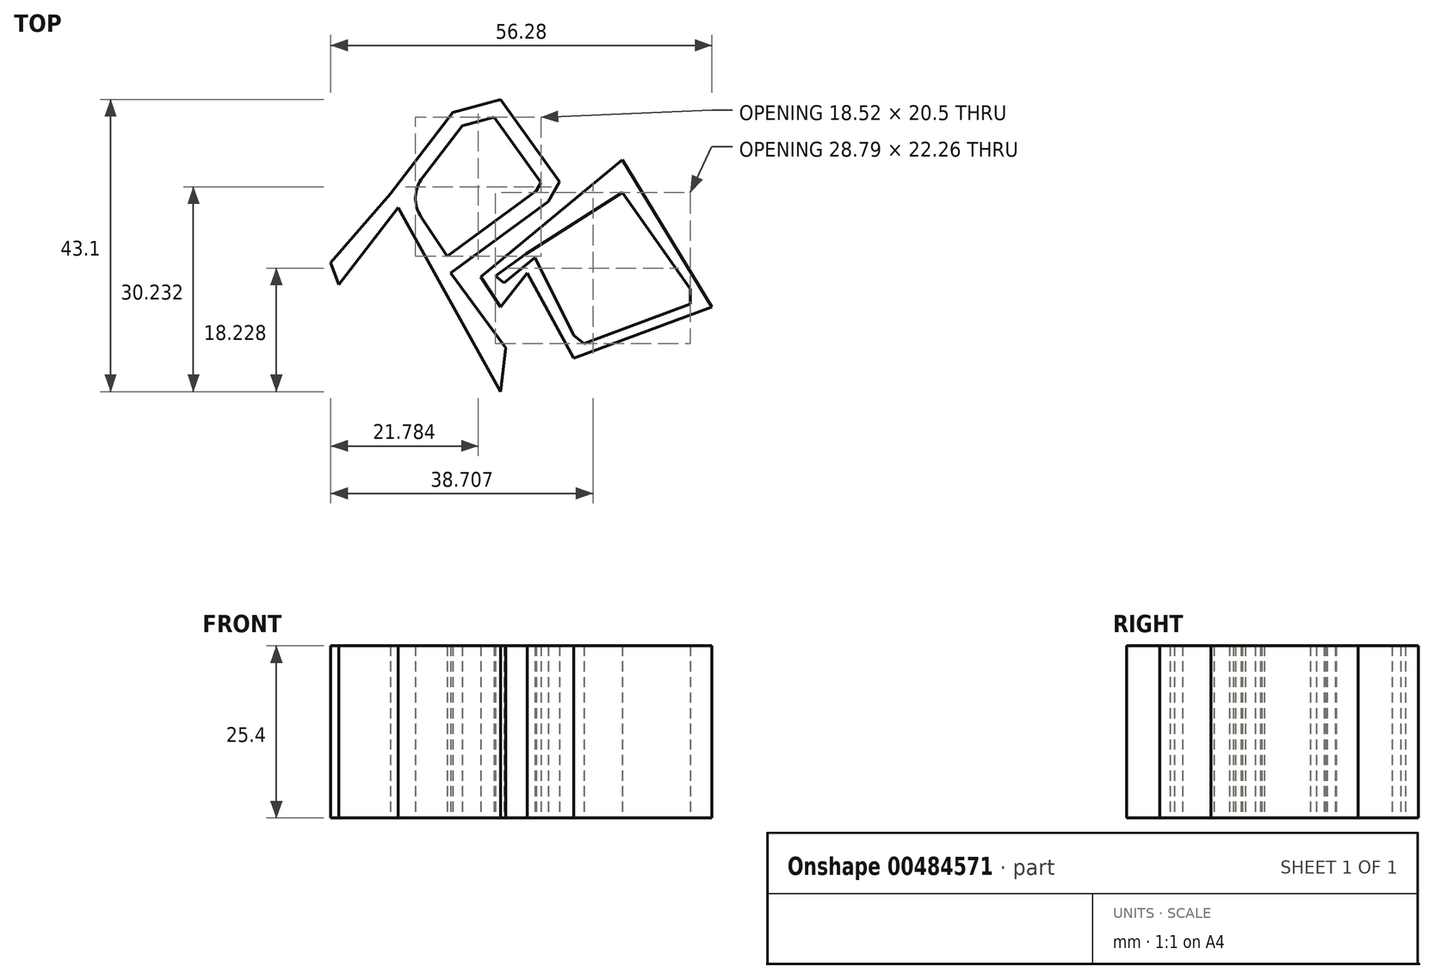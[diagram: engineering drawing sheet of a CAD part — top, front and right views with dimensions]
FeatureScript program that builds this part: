
annotation { "Feature Type Name" : "Feature", "Feature Type Description" : "" }
export const myFeature = defineFeature(function(context is Context, id is Id, definition is map)
    precondition{}
    {
        {
            var Q0;
            Q0=qCreatedBy(makeId("Top.planeOp"),FACE);
            var sketch = newSketch(context, id + "F0", { "sketchPlane" : qUnion([Q0])});
            skLineSegment(sketch, "E0", {"start": v(-7.9, -8.74) * mm, "end": v(-16.01, 2.35) * mm});
            skLineSegment(sketch, "E1", {"start": v(-16.01, 2.35) * mm, "end": v(-1.64, 12.87) * mm});
            skLineSegment(sketch, "E2", {"start": v(-1.64, 12.87) * mm, "end": v(0, 15.8) * mm});
            skLineSegment(sketch, "E3", {"start": v(0, 15.8) * mm, "end": v(-8.69, 27.92) * mm});
            skLineSegment(sketch, "E4", {"start": v(-8.69, 27.92) * mm, "end": v(-15.7, 26.02) * mm});
            skLineSegment(sketch, "E5", {"start": v(-15.7, 26.02) * mm, "end": v(-24.95, 13.99) * mm});
            skLineSegment(sketch, "E6", {"start": v(-23.82, 11.95) * mm, "end": v(-8.69, -15.18) * mm});
            skLineSegment(sketch, "E7", {"start": v(-8.69, -15.18) * mm, "end": v(-7.9, -8.74) * mm});
            skLineSegment(sketch, "E8", {"start": v(-11.57, 1.75) * mm, "end": v(9.32, 19.04) * mm});
            skLineSegment(sketch, "E9", {"start": v(9.32, 19.04) * mm, "end": v(22.53, -2.7) * mm});
            skLineSegment(sketch, "E10", {"start": v(22.53, -2.7) * mm, "end": v(2.12, -10.26) * mm});
            skLineSegment(sketch, "E11", {"start": v(2.12, -10.26) * mm, "end": v(-4.72, 2.35) * mm});
            skLineSegment(sketch, "E12", {"start": v(-4.72, 2.35) * mm, "end": v(-8.69, -2.7) * mm});
            skLineSegment(sketch, "E13", {"start": v(-8.69, -2.7) * mm, "end": v(-11.57, 1.75) * mm});
            skLineSegment(sketch, "E14", {"start": v(-24.95, 13.99) * mm, "end": v(-33.75, 3.86) * mm});
            skLineSegment(sketch, "E15", {"start": v(-33.75, 3.86) * mm, "end": v(-32.54, 0.6) * mm});
            skLineSegment(sketch, "E16", {"start": v(-32.54, 0.6) * mm, "end": v(-23.82, 11.95) * mm});
            skLineSegment(sketch, "E17.0", {"start": v(-14.36, 24.02) * mm, "end": v(-22.4, 13.55) * mm});
            skLineSegment(sketch, "E17.1", {"start": v(-16.53, 4.8) * mm, "end": v(-3.4, 14.42) * mm});
            skLineSegment(sketch, "E17.2", {"start": v(-3.4, 14.42) * mm, "end": v(-2.7, 15.65) * mm});
            skLineSegment(sketch, "E17.3", {"start": v(-2.7, 15.65) * mm, "end": v(-9.62, 25.3) * mm});
            skLineSegment(sketch, "E17.4", {"start": v(-9.62, 25.3) * mm, "end": v(-14.36, 24.02) * mm});
            skLineSegment(sketch, "E18", {"start": v(-16.53, 4.8) * mm, "end": v(-22.4, 13.55) * mm});
            skLineSegment(sketch, "E19", {"start": v(2.13, -6.88) * mm, "end": v(3.66, -8.08) * mm});
            skLineSegment(sketch, "E20", {"start": v(3.66, -8.08) * mm, "end": v(19.35, -2.27) * mm});
            skLineSegment(sketch, "E21", {"start": v(19.35, -2.27) * mm, "end": v(19.35, 0) * mm});
            skLineSegment(sketch, "E22", {"start": v(19.35, 0) * mm, "end": v(9.27, 14.18) * mm});
            skLineSegment(sketch, "E23", {"start": v(9.27, 14.18) * mm, "end": v(-4.87, 5.18) * mm});
            skLineSegment(sketch, "E24", {"start": v(-4.87, 5.18) * mm, "end": v(-9.44, 1.9) * mm});
            skLineSegment(sketch, "E25", {"start": v(-9.44, 1.9) * mm, "end": v(-8.15, 0.89) * mm});
            skLineSegment(sketch, "E26", {"start": v(-8.15, 0.89) * mm, "end": v(-3.58, 4.61) * mm});
            skLineSegment(sketch, "E27", {"start": v(-3.58, 4.61) * mm, "end": v(2.13, -6.88) * mm});
            skLineSegment(sketch, "E28", {"start": v(-41.15, -4.64) * mm, "end": v(29.13, -28.62) * mm});
            skLineSegment(sketch, "E29.MirrorCS", {"start": v(-22.92, -42.8) * mm, "end": v(-23.12, -44.2) * mm});
            skLineSegment(sketch, "E30.MirrorCS", {"start": v(-20.05, -29.2) * mm, "end": v(-18.41, -29.19) * mm});
            skLineSegment(sketch, "E31.MirrorCS", {"start": v(-5.53, -29.32) * mm, "end": v(-3.58, -29.3) * mm});
            skLineSegment(sketch, "E32.MirrorCS", {"start": v(-12.33, -21.72) * mm, "end": v(-25.53, -25.54) * mm});
            skLineSegment(sketch, "E33.MirrorCS", {"start": v(-25.53, -25.54) * mm, "end": v(-20.58, -42.65) * mm});
            skLineSegment(sketch, "E34.MirrorCS", {"start": v(-21.08, -45.97) * mm, "end": v(-35.36, -50.26) * mm});
            skLineSegment(sketch, "E35.MirrorCS", {"start": v(-27.44, -27.16) * mm, "end": v(-37.43, -30.5) * mm});
            skLineSegment(sketch, "E36.MirrorCS", {"start": v(-37.58, -28.37) * mm, "end": v(-9.02, -16.14) * mm});
            skLineSegment(sketch, "E37.MirrorCS", {"start": v(-9.02, -16.14) * mm, "end": v(-12.33, -21.72) * mm});
            skLineSegment(sketch, "E38.MirrorCS", {"start": v(-3.47, -26.64) * mm, "end": v(-16.6, -32.44) * mm});
            skLineSegment(sketch, "E39.MirrorCS", {"start": v(-17.08, -34.93) * mm, "end": v(-5.53, -29.32) * mm});
            skLineSegment(sketch, "E40.MirrorCS", {"start": v(-37.54, -14.05) * mm, "end": v(-37.58, -28.37) * mm});
            skLineSegment(sketch, "E41.MirrorCS", {"start": v(-18.44, -34.6) * mm, "end": v(-20.05, -29.2) * mm});
            skLineSegment(sketch, "E42.MirrorCS", {"start": v(-3.58, -29.3) * mm, "end": v(5.28, -43.5) * mm});
            skLineSegment(sketch, "E43.MirrorCS", {"start": v(-37.46, -43.7) * mm, "end": v(-37.43, -30.5) * mm});
            skLineSegment(sketch, "E44.MirrorCS", {"start": v(-16.65, -26.02) * mm, "end": v(-21.64, -27.78) * mm});
            skLineSegment(sketch, "E45.MirrorCS", {"start": v(5.28, -43.5) * mm, "end": v(3.9, -45.3) * mm});
            skLineSegment(sketch, "E46.MirrorCS", {"start": v(-40.49, -15.89) * mm, "end": v(-37.54, -14.05) * mm});
            skLineSegment(sketch, "E47.MirrorCS", {"start": v(-27.44, -27.16) * mm, "end": v(-22.92, -42.8) * mm});
            skLineSegment(sketch, "E48.MirrorCS", {"start": v(-20.58, -42.65) * mm, "end": v(-21.08, -45.97) * mm});
            skLineSegment(sketch, "E49.MirrorCS", {"start": v(-39.71, -29.29) * mm, "end": v(-40.49, -15.89) * mm});
            skLineSegment(sketch, "E50.MirrorCS", {"start": v(3.9, -45.3) * mm, "end": v(-12.75, -50.35) * mm});
            skLineSegment(sketch, "E51.MirrorCS", {"start": v(-35.36, -50.26) * mm, "end": v(-39.75, -44.47) * mm});
            skLineSegment(sketch, "E52.MirrorCS", {"start": v(-39.75, -44.47) * mm, "end": v(-39.71, -29.29) * mm});
            skLineSegment(sketch, "E53.MirrorCS", {"start": v(-21.64, -27.78) * mm, "end": v(-15.68, -54.23) * mm});
            skLineSegment(sketch, "E54.MirrorCS", {"start": v(-15.68, -54.23) * mm, "end": v(8.06, -45.1) * mm});
            skLineSegment(sketch, "E55.MirrorCS", {"start": v(8.06, -45.1) * mm, "end": v(-3.47, -26.64) * mm});
            skLineSegment(sketch, "E56.MirrorCS", {"start": v(-12.75, -50.35) * mm, "end": v(-18.44, -34.6) * mm});
            skLineSegment(sketch, "E57.MirrorCS", {"start": v(-16.6, -32.44) * mm, "end": v(-16.65, -26.02) * mm});
            skLineSegment(sketch, "E58.MirrorCS", {"start": v(-23.12, -44.2) * mm, "end": v(-34.5, -47.6) * mm});
            skLineSegment(sketch, "E59.MirrorCS", {"start": v(-34.5, -47.6) * mm, "end": v(-37.46, -43.7) * mm});
            skLineSegment(sketch, "E60.MirrorCS", {"start": v(-18.41, -29.19) * mm, "end": v(-17.08, -34.93) * mm});
            skSolve(sketch);
        }
        {
            var Q0;
            Q0=makeQuery(id+"F0.imprint","IMPRINT",FACE,{"disambiguationData":[TD([[makeQuery(id+"F0.imprint","IMPRINT",EDGE,{"derivedFrom":sQuery(id+"F0.wireOp",EDGE,"E0")}),1.0]])]});
            var Q1;
            Q1=makeQuery(id+"F0.imprint","IMPRINT",FACE,{"disambiguationData":[TD([[makeQuery(id+"F0.imprint","IMPRINT",EDGE,{"derivedFrom":sQuery(id+"F0.wireOp",EDGE,"E8")}),-1.0]])]});
            extrude(context, id + "F1", {"entities" : qUnion([Q0, Q1]), "depth" : 25.4 * mm});
        }
        {
            var Q0;
            Q0=makeQuery(id+"F1.opExtrude","SWEPT_EDGE",EDGE,{"disambiguationData":[OSD([sQuery(id+"F0.wireOp",EDGE,"E17.0"),sQuery(id+"F0.wireOp",EDGE,"E18")])]});
            fillet(context, id + "F2", {"entities" : qUnion([Q0]), "radius" : 5.08 * mm, "tangentPropagation" : true, "allowEdgeOverflow" : false});
        }
    });
